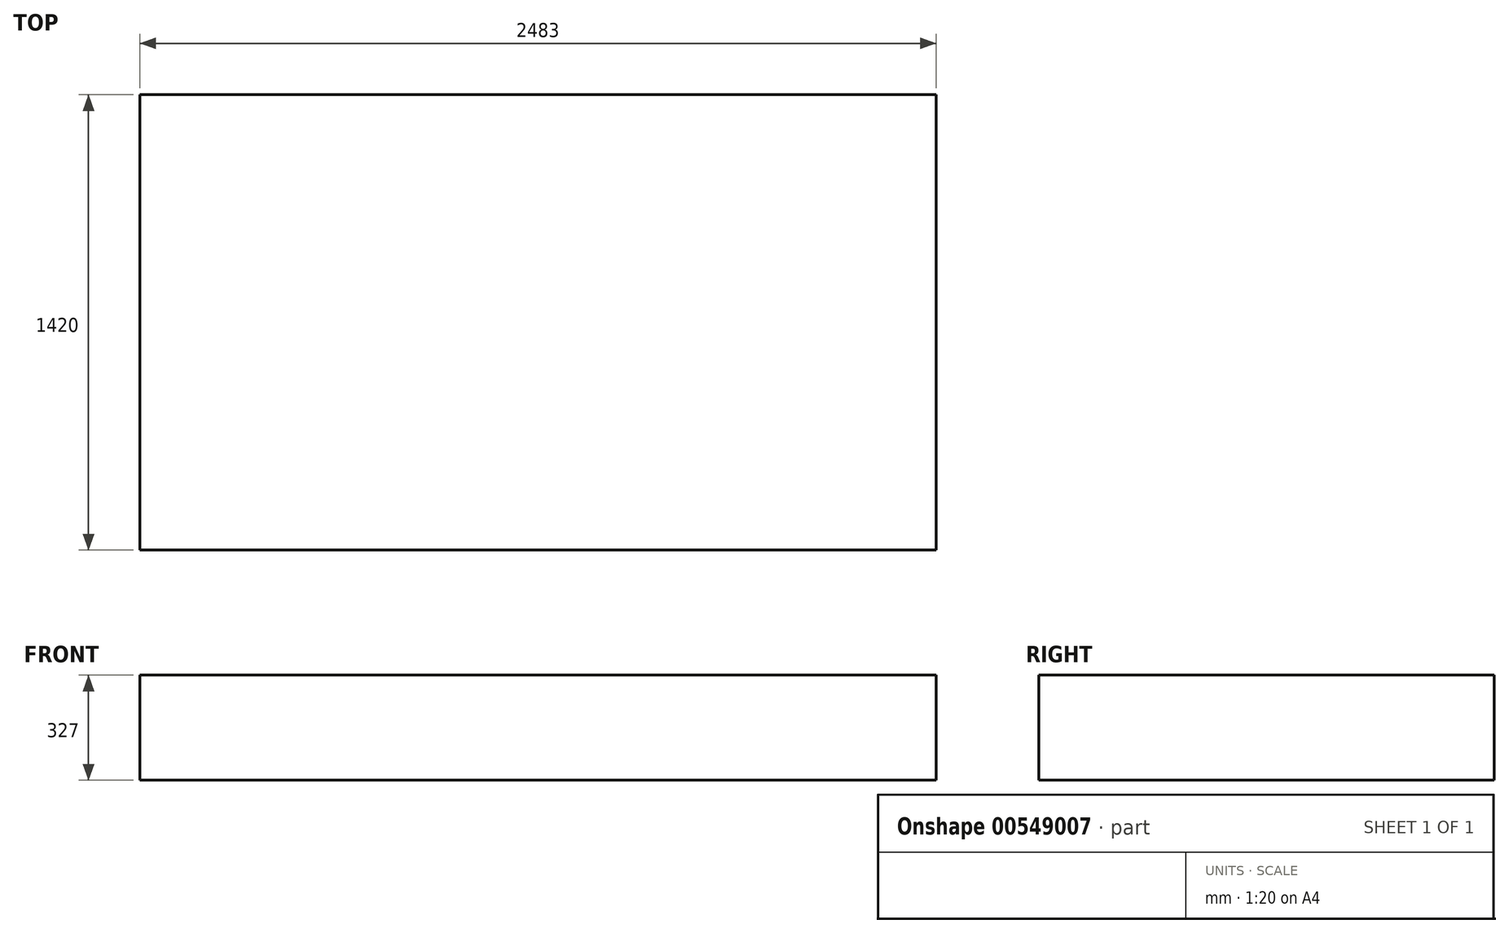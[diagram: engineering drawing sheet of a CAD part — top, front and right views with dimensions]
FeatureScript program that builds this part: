
annotation { "Feature Type Name" : "Feature", "Feature Type Description" : "" }
export const myFeature = defineFeature(function(context is Context, id is Id, definition is map)
    precondition{}
    {
        {
            var Q0;
            Q0=qCreatedBy(makeId("Top.planeOp"),FACE);
            var sketch = newSketch(context, id + "F0", { "sketchPlane" : qUnion([Q0])});
            skLineSegment(sketch, "E0.bottom", {"start": v(1241.5, -710) * mm, "end": v(-1241.5, -710) * mm});
            skLineSegment(sketch, "E0.top", {"start": v(1241.5, 710) * mm, "end": v(-1241.5, 710) * mm});
            skLineSegment(sketch, "E0.left", {"start": v(1241.5, -710) * mm, "end": v(1241.5, 710) * mm});
            skLineSegment(sketch, "E0.right", {"start": v(-1241.5, -710) * mm, "end": v(-1241.5, 710) * mm});
            skPoint(sketch, "E0.middle", {"position": v(0, 0) * mm});
            skSolve(sketch);
        }
        {
            var Q0;
            Q0=makeQuery(id+"F0.imprint","IMPRINT",FACE,{"disambiguationData":[TD([[makeQuery(id+"F0.imprint","IMPRINT",EDGE,{"derivedFrom":sQuery(id+"F0.wireOp",EDGE,"E0.bottom")}),-1.0]])]});
            extrude(context, id + "F1", {"entities" : qUnion([Q0]), "depth" : 327 * mm, "offsetDistance" : 25 * mm});
        }
    });
